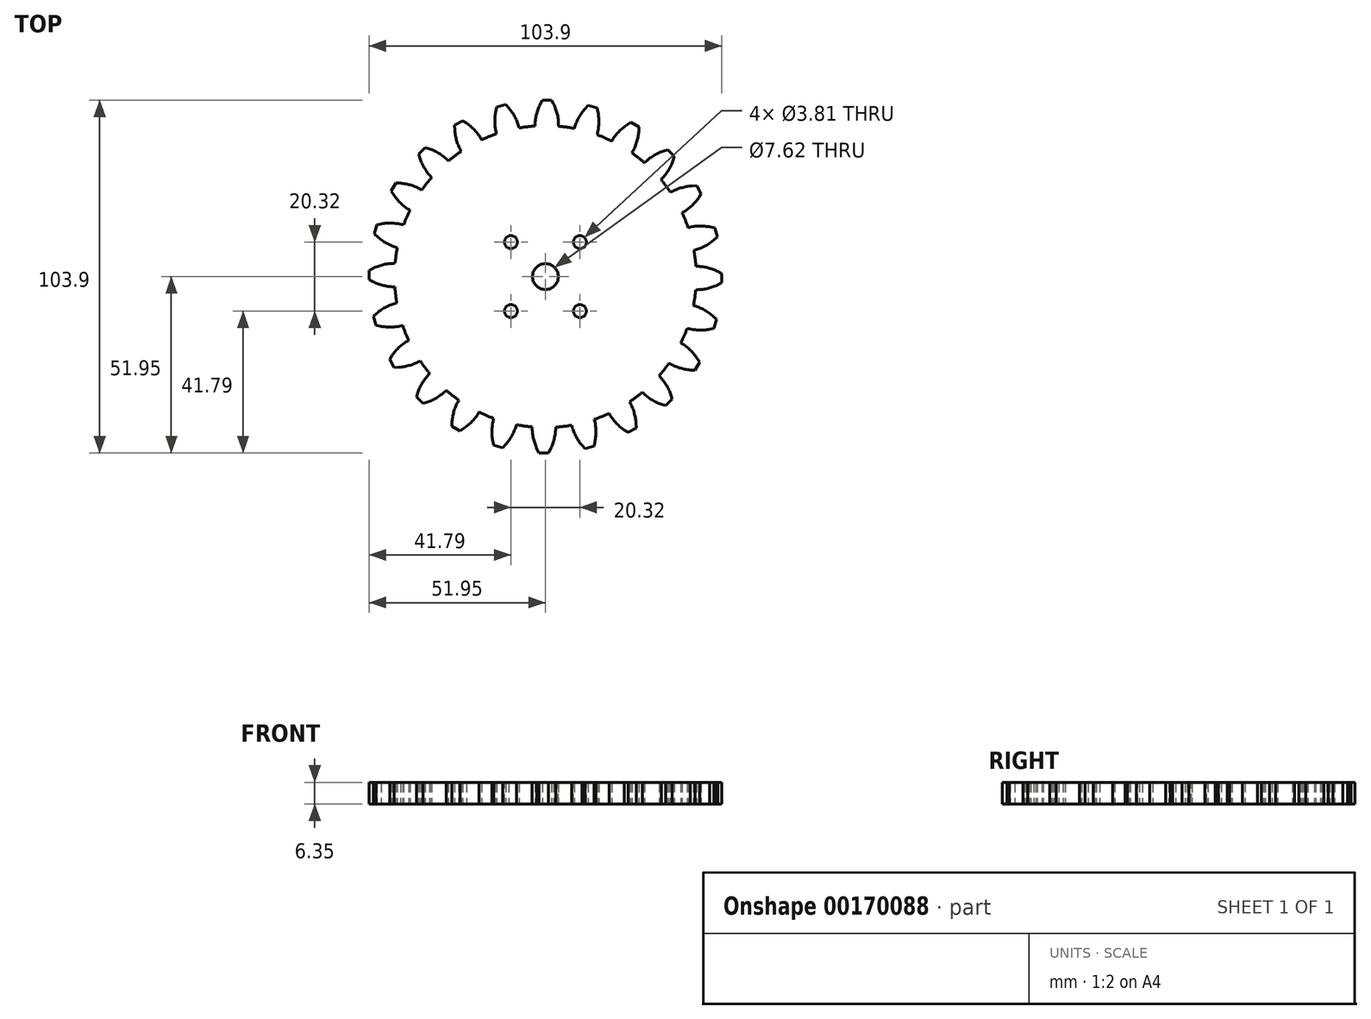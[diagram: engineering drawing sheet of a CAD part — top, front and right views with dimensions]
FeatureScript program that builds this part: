
annotation { "Feature Type Name" : "Feature", "Feature Type Description" : "" }
export const myFeature = defineFeature(function(context is Context, id is Id, definition is map)
    precondition{}
    {
        {
            var Q0;
            Q0=qCreatedBy(makeId("Top.planeOp"),FACE);
            var sketch = newSketch(context, id + "F0", { "sketchPlane" : qUnion([Q0])});
            skCircle(sketch, "E0", {"center": v(0, 0) * mm, "radius": 44.45 * mm});
            skCircle(sketch, "E1", {"center": v(0, 0) * mm, "radius": 47.63 * mm, "construction": true});
            skCircle(sketch, "E2", {"center": v(0, 0) * mm, "radius": 50.8 * mm, "construction": true});
            skLineSegment(sketch, "E3", {"start": v(74.5, -50.8) * mm, "end": v(0, 0) * mm, "construction": true});
            skLineSegment(sketch, "E4", {"start": v(0, 0) * mm, "end": v(77.18, -45.55) * mm, "construction": true});
            skLineSegment(sketch, "E5", {"start": v(39.35, -26.83) * mm, "end": v(73.48, 16.73) * mm, "construction": true});
            skLineSegment(sketch, "E6", {"start": v(39.35, -26.83) * mm, "end": v(56.8, 26.67) * mm, "construction": true});
            skCircle(sketch, "E7", {"center": v(39.35, -26.83) * mm, "radius": 14.6 * mm, "construction": true});
            skArc(sketch, "E8", {"start": v(36.25, -25.4) * mm, "mid": v(39.35, -26.84) * mm, "end": v(42.7, -27.5) * mm});
            skPoint(sketch, "E8.startSnap0", {"position": v(37.25, -25.4) * mm});
            skArc(sketch, "E9.MirrorCS", {"start": v(39.76, -19.45) * mm, "mid": v(42.52, -21.47) * mm, "end": v(44.73, -24.09) * mm});
            skLineSegment(sketch, "E10", {"start": v(44.73, -24.09) * mm, "end": v(45.45, -25.17) * mm});
            skLineSegment(sketch, "E11", {"start": v(45.45, -25.17) * mm, "end": v(44.04, -27.55) * mm});
            skLineSegment(sketch, "E12", {"start": v(44.04, -27.55) * mm, "end": v(42.7, -27.5) * mm});
            skArc(sketch, "E13.1.0", {"start": v(43.44, -8.5) * mm, "mid": v(46.63, -9.74) * mm, "end": v(49.44, -11.69) * mm});
            skLineSegment(sketch, "E13.1.1", {"start": v(49.44, -11.69) * mm, "end": v(50.41, -12.55) * mm});
            skLineSegment(sketch, "E13.1.2", {"start": v(50.41, -12.55) * mm, "end": v(49.67, -15.21) * mm});
            skLineSegment(sketch, "E13.1.3", {"start": v(49.67, -15.21) * mm, "end": v(48.37, -15.52) * mm});
            skArc(sketch, "E13.1.4", {"start": v(41.59, -15.16) * mm, "mid": v(44.96, -15.74) * mm, "end": v(48.37, -15.52) * mm});
            skArc(sketch, "E13.2.0", {"start": v(44.16, 3.04) * mm, "mid": v(47.56, 2.66) * mm, "end": v(50.78, 1.5) * mm});
            skLineSegment(sketch, "E13.2.1", {"start": v(50.78, 1.5) * mm, "end": v(51.95, 0.92) * mm});
            skLineSegment(sketch, "E13.2.2", {"start": v(51.95, 0.92) * mm, "end": v(51.92, -1.84) * mm});
            skLineSegment(sketch, "E13.2.3", {"start": v(51.92, -1.84) * mm, "end": v(50.74, -2.47) * mm});
            skArc(sketch, "E13.2.4", {"start": v(44.1, -3.88) * mm, "mid": v(47.5, -3.56) * mm, "end": v(50.74, -2.47) * mm});
            skArc(sketch, "E13.3.0", {"start": v(41.87, 14.36) * mm, "mid": v(45.25, 14.88) * mm, "end": v(48.66, 14.6) * mm});
            skLineSegment(sketch, "E13.3.1", {"start": v(48.66, 14.6) * mm, "end": v(49.94, 14.34) * mm});
            skLineSegment(sketch, "E13.3.2", {"start": v(49.94, 14.34) * mm, "end": v(50.63, 11.66) * mm});
            skLineSegment(sketch, "E13.3.3", {"start": v(50.63, 11.66) * mm, "end": v(49.65, 10.75) * mm});
            skArc(sketch, "E13.3.4", {"start": v(43.6, 7.67) * mm, "mid": v(46.8, 8.85) * mm, "end": v(49.65, 10.75) * mm});
            skArc(sketch, "E13.4.0", {"start": v(36.72, 24.71) * mm, "mid": v(39.86, 26.08) * mm, "end": v(43.22, 26.7) * mm});
            skLineSegment(sketch, "E13.4.1", {"start": v(43.22, 26.7) * mm, "end": v(44.52, 26.77) * mm});
            skLineSegment(sketch, "E13.4.2", {"start": v(44.52, 26.77) * mm, "end": v(45.88, 24.37) * mm});
            skLineSegment(sketch, "E13.4.3", {"start": v(45.88, 24.37) * mm, "end": v(45.18, 23.23) * mm});
            skArc(sketch, "E13.4.4", {"start": v(40.12, 18.7) * mm, "mid": v(42.92, 20.66) * mm, "end": v(45.18, 23.23) * mm});
            skArc(sketch, "E13.5.0", {"start": v(29.08, 33.37) * mm, "mid": v(31.75, 35.51) * mm, "end": v(34.84, 36.97) * mm});
            skLineSegment(sketch, "E13.5.1", {"start": v(34.84, 36.97) * mm, "end": v(36.08, 37.38) * mm});
            skLineSegment(sketch, "E13.5.2", {"start": v(36.08, 37.38) * mm, "end": v(38.01, 35.41) * mm});
            skLineSegment(sketch, "E13.5.3", {"start": v(38.01, 35.41) * mm, "end": v(37.62, 34.13) * mm});
            skArc(sketch, "E13.5.4", {"start": v(33.92, 28.44) * mm, "mid": v(36.1, 31.07) * mm, "end": v(37.62, 34.13) * mm});
            skArc(sketch, "E13.6.0", {"start": v(19.45, 39.76) * mm, "mid": v(21.47, 42.52) * mm, "end": v(24.09, 44.73) * mm});
            skLineSegment(sketch, "E13.6.1", {"start": v(24.09, 44.73) * mm, "end": v(25.17, 45.45) * mm});
            skLineSegment(sketch, "E13.6.2", {"start": v(25.17, 45.45) * mm, "end": v(27.55, 44.04) * mm});
            skLineSegment(sketch, "E13.6.3", {"start": v(27.55, 44.04) * mm, "end": v(27.5, 42.7) * mm});
            skArc(sketch, "E13.6.4", {"start": v(25.4, 36.25) * mm, "mid": v(26.84, 39.35) * mm, "end": v(27.5, 42.7) * mm});
            skArc(sketch, "E13.7.0", {"start": v(8.5, 43.44) * mm, "mid": v(9.74, 46.63) * mm, "end": v(11.69, 49.44) * mm});
            skLineSegment(sketch, "E13.7.1", {"start": v(11.69, 49.44) * mm, "end": v(12.55, 50.41) * mm});
            skLineSegment(sketch, "E13.7.2", {"start": v(12.55, 50.41) * mm, "end": v(15.21, 49.67) * mm});
            skLineSegment(sketch, "E13.7.3", {"start": v(15.21, 49.67) * mm, "end": v(15.52, 48.37) * mm});
            skArc(sketch, "E13.7.4", {"start": v(15.16, 41.59) * mm, "mid": v(15.74, 44.96) * mm, "end": v(15.52, 48.37) * mm});
            skArc(sketch, "E13.8.0", {"start": v(-3.04, 44.16) * mm, "mid": v(-2.66, 47.56) * mm, "end": v(-1.5, 50.78) * mm});
            skLineSegment(sketch, "E13.8.1", {"start": v(-1.5, 50.78) * mm, "end": v(-0.92, 51.95) * mm});
            skLineSegment(sketch, "E13.8.2", {"start": v(-0.92, 51.95) * mm, "end": v(1.84, 51.92) * mm});
            skLineSegment(sketch, "E13.8.3", {"start": v(1.84, 51.92) * mm, "end": v(2.47, 50.74) * mm});
            skArc(sketch, "E13.8.4", {"start": v(3.88, 44.1) * mm, "mid": v(3.56, 47.5) * mm, "end": v(2.47, 50.74) * mm});
            skArc(sketch, "E13.9.0", {"start": v(-14.36, 41.87) * mm, "mid": v(-14.88, 45.25) * mm, "end": v(-14.6, 48.66) * mm});
            skLineSegment(sketch, "E13.9.1", {"start": v(-14.6, 48.66) * mm, "end": v(-14.34, 49.94) * mm});
            skLineSegment(sketch, "E13.9.2", {"start": v(-14.34, 49.94) * mm, "end": v(-11.66, 50.63) * mm});
            skLineSegment(sketch, "E13.9.3", {"start": v(-11.66, 50.63) * mm, "end": v(-10.75, 49.65) * mm});
            skArc(sketch, "E13.9.4", {"start": v(-7.67, 43.6) * mm, "mid": v(-8.85, 46.8) * mm, "end": v(-10.75, 49.65) * mm});
            skArc(sketch, "E13.10.0", {"start": v(-24.71, 36.72) * mm, "mid": v(-26.08, 39.86) * mm, "end": v(-26.7, 43.22) * mm});
            skLineSegment(sketch, "E13.10.1", {"start": v(-26.7, 43.22) * mm, "end": v(-26.77, 44.52) * mm});
            skLineSegment(sketch, "E13.10.2", {"start": v(-26.77, 44.52) * mm, "end": v(-24.37, 45.88) * mm});
            skLineSegment(sketch, "E13.10.3", {"start": v(-24.37, 45.88) * mm, "end": v(-23.23, 45.18) * mm});
            skArc(sketch, "E13.10.4", {"start": v(-18.7, 40.12) * mm, "mid": v(-20.66, 42.92) * mm, "end": v(-23.23, 45.18) * mm});
            skArc(sketch, "E13.11.0", {"start": v(-33.37, 29.08) * mm, "mid": v(-35.51, 31.75) * mm, "end": v(-36.97, 34.84) * mm});
            skLineSegment(sketch, "E13.11.1", {"start": v(-36.97, 34.84) * mm, "end": v(-37.38, 36.08) * mm});
            skLineSegment(sketch, "E13.11.2", {"start": v(-37.38, 36.08) * mm, "end": v(-35.41, 38.01) * mm});
            skLineSegment(sketch, "E13.11.3", {"start": v(-35.41, 38.01) * mm, "end": v(-34.13, 37.62) * mm});
            skArc(sketch, "E13.11.4", {"start": v(-28.44, 33.92) * mm, "mid": v(-31.07, 36.1) * mm, "end": v(-34.13, 37.62) * mm});
            skArc(sketch, "E13.12.0", {"start": v(-39.76, 19.45) * mm, "mid": v(-42.52, 21.47) * mm, "end": v(-44.73, 24.09) * mm});
            skLineSegment(sketch, "E13.12.1", {"start": v(-44.73, 24.09) * mm, "end": v(-45.45, 25.17) * mm});
            skLineSegment(sketch, "E13.12.2", {"start": v(-45.45, 25.17) * mm, "end": v(-44.04, 27.55) * mm});
            skLineSegment(sketch, "E13.12.3", {"start": v(-44.04, 27.55) * mm, "end": v(-42.7, 27.5) * mm});
            skArc(sketch, "E13.12.4", {"start": v(-36.25, 25.4) * mm, "mid": v(-39.35, 26.84) * mm, "end": v(-42.7, 27.5) * mm});
            skArc(sketch, "E13.13.0", {"start": v(-43.44, 8.5) * mm, "mid": v(-46.63, 9.74) * mm, "end": v(-49.44, 11.69) * mm});
            skLineSegment(sketch, "E13.13.1", {"start": v(-49.44, 11.69) * mm, "end": v(-50.41, 12.55) * mm});
            skLineSegment(sketch, "E13.13.2", {"start": v(-50.41, 12.55) * mm, "end": v(-49.67, 15.21) * mm});
            skLineSegment(sketch, "E13.13.3", {"start": v(-49.67, 15.21) * mm, "end": v(-48.37, 15.52) * mm});
            skArc(sketch, "E13.13.4", {"start": v(-41.59, 15.16) * mm, "mid": v(-44.96, 15.74) * mm, "end": v(-48.37, 15.52) * mm});
            skArc(sketch, "E13.14.0", {"start": v(-44.16, -3.04) * mm, "mid": v(-47.56, -2.66) * mm, "end": v(-50.78, -1.5) * mm});
            skLineSegment(sketch, "E13.14.1", {"start": v(-50.78, -1.5) * mm, "end": v(-51.95, -0.92) * mm});
            skLineSegment(sketch, "E13.14.2", {"start": v(-51.95, -0.92) * mm, "end": v(-51.92, 1.84) * mm});
            skLineSegment(sketch, "E13.14.3", {"start": v(-51.92, 1.84) * mm, "end": v(-50.74, 2.47) * mm});
            skArc(sketch, "E13.14.4", {"start": v(-44.1, 3.88) * mm, "mid": v(-47.5, 3.56) * mm, "end": v(-50.74, 2.47) * mm});
            skArc(sketch, "E13.15.0", {"start": v(-41.87, -14.36) * mm, "mid": v(-45.25, -14.88) * mm, "end": v(-48.66, -14.6) * mm});
            skLineSegment(sketch, "E13.15.1", {"start": v(-48.66, -14.6) * mm, "end": v(-49.94, -14.34) * mm});
            skLineSegment(sketch, "E13.15.2", {"start": v(-49.94, -14.34) * mm, "end": v(-50.63, -11.66) * mm});
            skLineSegment(sketch, "E13.15.3", {"start": v(-50.63, -11.66) * mm, "end": v(-49.65, -10.75) * mm});
            skArc(sketch, "E13.15.4", {"start": v(-43.6, -7.67) * mm, "mid": v(-46.8, -8.85) * mm, "end": v(-49.65, -10.75) * mm});
            skArc(sketch, "E13.16.0", {"start": v(-36.72, -24.71) * mm, "mid": v(-39.86, -26.08) * mm, "end": v(-43.22, -26.7) * mm});
            skLineSegment(sketch, "E13.16.1", {"start": v(-43.22, -26.7) * mm, "end": v(-44.52, -26.77) * mm});
            skLineSegment(sketch, "E13.16.2", {"start": v(-44.52, -26.77) * mm, "end": v(-45.88, -24.37) * mm});
            skLineSegment(sketch, "E13.16.3", {"start": v(-45.88, -24.37) * mm, "end": v(-45.18, -23.23) * mm});
            skArc(sketch, "E13.16.4", {"start": v(-40.12, -18.7) * mm, "mid": v(-42.92, -20.66) * mm, "end": v(-45.18, -23.23) * mm});
            skArc(sketch, "E13.17.0", {"start": v(-29.08, -33.37) * mm, "mid": v(-31.75, -35.51) * mm, "end": v(-34.84, -36.97) * mm});
            skLineSegment(sketch, "E13.17.1", {"start": v(-34.84, -36.97) * mm, "end": v(-36.08, -37.38) * mm});
            skLineSegment(sketch, "E13.17.2", {"start": v(-36.08, -37.38) * mm, "end": v(-38.01, -35.41) * mm});
            skLineSegment(sketch, "E13.17.3", {"start": v(-38.01, -35.41) * mm, "end": v(-37.62, -34.13) * mm});
            skArc(sketch, "E13.17.4", {"start": v(-33.92, -28.44) * mm, "mid": v(-36.1, -31.07) * mm, "end": v(-37.62, -34.13) * mm});
            skArc(sketch, "E13.18.0", {"start": v(-19.45, -39.76) * mm, "mid": v(-21.47, -42.52) * mm, "end": v(-24.09, -44.73) * mm});
            skLineSegment(sketch, "E13.18.1", {"start": v(-24.09, -44.73) * mm, "end": v(-25.17, -45.45) * mm});
            skLineSegment(sketch, "E13.18.2", {"start": v(-25.17, -45.45) * mm, "end": v(-27.55, -44.04) * mm});
            skLineSegment(sketch, "E13.18.3", {"start": v(-27.55, -44.04) * mm, "end": v(-27.5, -42.7) * mm});
            skArc(sketch, "E13.18.4", {"start": v(-25.4, -36.25) * mm, "mid": v(-26.84, -39.35) * mm, "end": v(-27.5, -42.7) * mm});
            skArc(sketch, "E13.19.0", {"start": v(-8.5, -43.44) * mm, "mid": v(-9.74, -46.63) * mm, "end": v(-11.69, -49.44) * mm});
            skLineSegment(sketch, "E13.19.1", {"start": v(-11.69, -49.44) * mm, "end": v(-12.55, -50.41) * mm});
            skLineSegment(sketch, "E13.19.2", {"start": v(-12.55, -50.41) * mm, "end": v(-15.21, -49.67) * mm});
            skLineSegment(sketch, "E13.19.3", {"start": v(-15.21, -49.67) * mm, "end": v(-15.52, -48.37) * mm});
            skArc(sketch, "E13.19.4", {"start": v(-15.16, -41.59) * mm, "mid": v(-15.74, -44.96) * mm, "end": v(-15.52, -48.37) * mm});
            skArc(sketch, "E13.20.0", {"start": v(3.04, -44.16) * mm, "mid": v(2.66, -47.56) * mm, "end": v(1.5, -50.78) * mm});
            skLineSegment(sketch, "E13.20.1", {"start": v(1.5, -50.78) * mm, "end": v(0.92, -51.95) * mm});
            skLineSegment(sketch, "E13.20.2", {"start": v(0.92, -51.95) * mm, "end": v(-1.84, -51.92) * mm});
            skLineSegment(sketch, "E13.20.3", {"start": v(-1.84, -51.92) * mm, "end": v(-2.47, -50.74) * mm});
            skArc(sketch, "E13.20.4", {"start": v(-3.88, -44.1) * mm, "mid": v(-3.56, -47.5) * mm, "end": v(-2.47, -50.74) * mm});
            skArc(sketch, "E13.21.0", {"start": v(14.36, -41.87) * mm, "mid": v(14.88, -45.25) * mm, "end": v(14.6, -48.66) * mm});
            skLineSegment(sketch, "E13.21.1", {"start": v(14.6, -48.66) * mm, "end": v(14.34, -49.94) * mm});
            skLineSegment(sketch, "E13.21.2", {"start": v(14.34, -49.94) * mm, "end": v(11.66, -50.63) * mm});
            skLineSegment(sketch, "E13.21.3", {"start": v(11.66, -50.63) * mm, "end": v(10.75, -49.65) * mm});
            skArc(sketch, "E13.21.4", {"start": v(7.67, -43.6) * mm, "mid": v(8.85, -46.8) * mm, "end": v(10.75, -49.65) * mm});
            skArc(sketch, "E13.22.0", {"start": v(24.71, -36.72) * mm, "mid": v(26.08, -39.86) * mm, "end": v(26.7, -43.22) * mm});
            skLineSegment(sketch, "E13.22.1", {"start": v(26.7, -43.22) * mm, "end": v(26.77, -44.52) * mm});
            skLineSegment(sketch, "E13.22.2", {"start": v(26.77, -44.52) * mm, "end": v(24.37, -45.88) * mm});
            skLineSegment(sketch, "E13.22.3", {"start": v(24.37, -45.88) * mm, "end": v(23.23, -45.18) * mm});
            skArc(sketch, "E13.22.4", {"start": v(18.7, -40.12) * mm, "mid": v(20.66, -42.92) * mm, "end": v(23.23, -45.18) * mm});
            skArc(sketch, "E13.23.0", {"start": v(33.37, -29.08) * mm, "mid": v(35.51, -31.75) * mm, "end": v(36.97, -34.84) * mm});
            skLineSegment(sketch, "E13.23.1", {"start": v(36.97, -34.84) * mm, "end": v(37.38, -36.08) * mm});
            skLineSegment(sketch, "E13.23.2", {"start": v(37.38, -36.08) * mm, "end": v(35.41, -38.01) * mm});
            skLineSegment(sketch, "E13.23.3", {"start": v(35.41, -38.01) * mm, "end": v(34.13, -37.62) * mm});
            skArc(sketch, "E13.23.4", {"start": v(28.44, -33.92) * mm, "mid": v(31.07, -36.1) * mm, "end": v(34.13, -37.62) * mm});
            skSolve(sketch);
        }
        {
            var Q0;
            {var subQ0=sQuery(id+"F0.wireOp",EDGE,"E0");var subQ30=makeQuery(id+"F0.imprint","INTERSECT",VERTEX,{"derivedFrom":[subQ0,sQuery(id+"F0.wireOp",EDGE,"E13.3.4")]});Q0=makeQuery(id+"F0.imprint","IMPRINT",FACE,{"disambiguationData":[TD([[makeQuery(id+"F0.imprint","IMPRINT",EDGE,{"disambiguationData":[TD([[subQ30,1.0]])],"derivedFrom":subQ0}),1.0]])]});}
            var Q1;
            {var subQ5=sQuery(id+"F0.wireOp",EDGE,"E13.13.1");Q1=makeQuery(id+"F0.imprint","IMPRINT",FACE,{"disambiguationData":[TD([[makeQuery(id+"F0.imprint","IMPRINT",EDGE,{"derivedFrom":subQ5}),-1.0]])]});}
            var Q2;
            {var subQ0=sQuery(id+"F0.wireOp",EDGE,"E13.12.1");Q2=makeQuery(id+"F0.imprint","IMPRINT",FACE,{"disambiguationData":[TD([[makeQuery(id+"F0.imprint","IMPRINT",EDGE,{"derivedFrom":subQ0}),-1.0]])]});}
            var Q3;
            {var subQ0=sQuery(id+"F0.wireOp",EDGE,"E13.11.1");Q3=makeQuery(id+"F0.imprint","IMPRINT",FACE,{"disambiguationData":[TD([[makeQuery(id+"F0.imprint","IMPRINT",EDGE,{"derivedFrom":subQ0}),-1.0]])]});}
            var Q4;
            {var subQ0=sQuery(id+"F0.wireOp",EDGE,"E13.10.1");Q4=makeQuery(id+"F0.imprint","IMPRINT",FACE,{"disambiguationData":[TD([[makeQuery(id+"F0.imprint","IMPRINT",EDGE,{"derivedFrom":subQ0}),-1.0]])]});}
            var Q5;
            {var subQ0=sQuery(id+"F0.wireOp",EDGE,"E13.9.1");Q5=makeQuery(id+"F0.imprint","IMPRINT",FACE,{"disambiguationData":[TD([[makeQuery(id+"F0.imprint","IMPRINT",EDGE,{"derivedFrom":subQ0}),-1.0]])]});}
            var Q6;
            {var subQ0=sQuery(id+"F0.wireOp",EDGE,"E13.8.1");Q6=makeQuery(id+"F0.imprint","IMPRINT",FACE,{"disambiguationData":[TD([[makeQuery(id+"F0.imprint","IMPRINT",EDGE,{"derivedFrom":subQ0}),-1.0]])]});}
            var Q7;
            {var subQ5=sQuery(id+"F0.wireOp",EDGE,"E13.7.1");Q7=makeQuery(id+"F0.imprint","IMPRINT",FACE,{"disambiguationData":[TD([[makeQuery(id+"F0.imprint","IMPRINT",EDGE,{"derivedFrom":subQ5}),-1.0]])]});}
            var Q8;
            {var subQ0=sQuery(id+"F0.wireOp",EDGE,"E13.6.1");Q8=makeQuery(id+"F0.imprint","IMPRINT",FACE,{"disambiguationData":[TD([[makeQuery(id+"F0.imprint","IMPRINT",EDGE,{"derivedFrom":subQ0}),-1.0]])]});}
            var Q9;
            {var subQ0=sQuery(id+"F0.wireOp",EDGE,"E13.5.1");Q9=makeQuery(id+"F0.imprint","IMPRINT",FACE,{"disambiguationData":[TD([[makeQuery(id+"F0.imprint","IMPRINT",EDGE,{"derivedFrom":subQ0}),-1.0]])]});}
            var Q10;
            {var subQ0=sQuery(id+"F0.wireOp",EDGE,"E13.4.1");Q10=makeQuery(id+"F0.imprint","IMPRINT",FACE,{"disambiguationData":[TD([[makeQuery(id+"F0.imprint","IMPRINT",EDGE,{"derivedFrom":subQ0}),-1.0]])]});}
            var Q11;
            {var subQ0=sQuery(id+"F0.wireOp",EDGE,"E13.3.1");Q11=makeQuery(id+"F0.imprint","IMPRINT",FACE,{"disambiguationData":[TD([[makeQuery(id+"F0.imprint","IMPRINT",EDGE,{"derivedFrom":subQ0}),-1.0]])]});}
            var Q12;
            {var subQ5=sQuery(id+"F0.wireOp",EDGE,"E13.2.1");Q12=makeQuery(id+"F0.imprint","IMPRINT",FACE,{"disambiguationData":[TD([[makeQuery(id+"F0.imprint","IMPRINT",EDGE,{"derivedFrom":subQ5}),-1.0]])]});}
            var Q13;
            {var subQ0=sQuery(id+"F0.wireOp",EDGE,"E13.1.1");Q13=makeQuery(id+"F0.imprint","IMPRINT",FACE,{"disambiguationData":[TD([[makeQuery(id+"F0.imprint","IMPRINT",EDGE,{"derivedFrom":subQ0}),-1.0]])]});}
            var Q14;
            {var subQ0=sQuery(id+"F0.wireOp",EDGE,"E10");Q14=makeQuery(id+"F0.imprint","IMPRINT",FACE,{"disambiguationData":[TD([[makeQuery(id+"F0.imprint","IMPRINT",EDGE,{"derivedFrom":subQ0}),-1.0]])]});}
            var Q15;
            {var subQ0=sQuery(id+"F0.wireOp",EDGE,"E13.23.1");Q15=makeQuery(id+"F0.imprint","IMPRINT",FACE,{"disambiguationData":[TD([[makeQuery(id+"F0.imprint","IMPRINT",EDGE,{"derivedFrom":subQ0}),-1.0]])]});}
            var Q16;
            {var subQ0=sQuery(id+"F0.wireOp",EDGE,"E13.22.1");Q16=makeQuery(id+"F0.imprint","IMPRINT",FACE,{"disambiguationData":[TD([[makeQuery(id+"F0.imprint","IMPRINT",EDGE,{"derivedFrom":subQ0}),-1.0]])]});}
            var Q17;
            {var subQ0=sQuery(id+"F0.wireOp",EDGE,"E13.21.1");Q17=makeQuery(id+"F0.imprint","IMPRINT",FACE,{"disambiguationData":[TD([[makeQuery(id+"F0.imprint","IMPRINT",EDGE,{"derivedFrom":subQ0}),-1.0]])]});}
            var Q18;
            {var subQ0=sQuery(id+"F0.wireOp",EDGE,"E13.20.1");Q18=makeQuery(id+"F0.imprint","IMPRINT",FACE,{"disambiguationData":[TD([[makeQuery(id+"F0.imprint","IMPRINT",EDGE,{"derivedFrom":subQ0}),-1.0]])]});}
            var Q19;
            {var subQ0=sQuery(id+"F0.wireOp",EDGE,"E13.19.1");Q19=makeQuery(id+"F0.imprint","IMPRINT",FACE,{"disambiguationData":[TD([[makeQuery(id+"F0.imprint","IMPRINT",EDGE,{"derivedFrom":subQ0}),-1.0]])]});}
            var Q20;
            {var subQ0=sQuery(id+"F0.wireOp",EDGE,"E13.18.1");Q20=makeQuery(id+"F0.imprint","IMPRINT",FACE,{"disambiguationData":[TD([[makeQuery(id+"F0.imprint","IMPRINT",EDGE,{"derivedFrom":subQ0}),-1.0]])]});}
            var Q21;
            {var subQ0=sQuery(id+"F0.wireOp",EDGE,"E13.17.1");Q21=makeQuery(id+"F0.imprint","IMPRINT",FACE,{"disambiguationData":[TD([[makeQuery(id+"F0.imprint","IMPRINT",EDGE,{"derivedFrom":subQ0}),-1.0]])]});}
            var Q22;
            {var subQ0=sQuery(id+"F0.wireOp",EDGE,"E13.16.1");Q22=makeQuery(id+"F0.imprint","IMPRINT",FACE,{"disambiguationData":[TD([[makeQuery(id+"F0.imprint","IMPRINT",EDGE,{"derivedFrom":subQ0}),-1.0]])]});}
            var Q23;
            {var subQ0=sQuery(id+"F0.wireOp",EDGE,"E13.15.1");Q23=makeQuery(id+"F0.imprint","IMPRINT",FACE,{"disambiguationData":[TD([[makeQuery(id+"F0.imprint","IMPRINT",EDGE,{"derivedFrom":subQ0}),-1.0]])]});}
            var Q24;
            {var subQ0=sQuery(id+"F0.wireOp",EDGE,"E13.14.1");Q24=makeQuery(id+"F0.imprint","IMPRINT",FACE,{"disambiguationData":[TD([[makeQuery(id+"F0.imprint","IMPRINT",EDGE,{"derivedFrom":subQ0}),-1.0]])]});}
            extrude(context, id + "F1", {"entities" : qUnion([Q0, Q1, Q2, Q3, Q4, Q5, Q6, Q7, Q8, Q9, Q10, Q11, Q12, Q13, Q14, Q15, Q16, Q17, Q18, Q19, Q20, Q21, Q22, Q23, Q24]), "depth" : 6.35 * mm});
        }
        {
            var Q0;
            Q0=makeQuery(id+"F1.opExtrude","CAP_FACE",FACE,{"disambiguationData":[OSD([sQuery(id+"F0.wireOp",EDGE,"E0"),sQuery(id+"F0.wireOp",EDGE,"E8"),sQuery(id+"F0.wireOp",EDGE,"E9.MirrorCS"),sQuery(id+"F0.wireOp",EDGE,"E10"),sQuery(id+"F0.wireOp",EDGE,"E11"),sQuery(id+"F0.wireOp",EDGE,"E12"),sQuery(id+"F0.wireOp",EDGE,"E13.1.0"),sQuery(id+"F0.wireOp",EDGE,"E13.1.1"),sQuery(id+"F0.wireOp",EDGE,"E13.1.2"),sQuery(id+"F0.wireOp",EDGE,"E13.1.3"),sQuery(id+"F0.wireOp",EDGE,"E13.1.4"),sQuery(id+"F0.wireOp",EDGE,"E13.2.0"),sQuery(id+"F0.wireOp",EDGE,"E13.2.1"),sQuery(id+"F0.wireOp",EDGE,"E13.2.2"),sQuery(id+"F0.wireOp",EDGE,"E13.2.3"),sQuery(id+"F0.wireOp",EDGE,"E13.2.4"),sQuery(id+"F0.wireOp",EDGE,"E13.3.0"),sQuery(id+"F0.wireOp",EDGE,"E13.3.1"),sQuery(id+"F0.wireOp",EDGE,"E13.3.2"),sQuery(id+"F0.wireOp",EDGE,"E13.3.3"),sQuery(id+"F0.wireOp",EDGE,"E13.3.4"),sQuery(id+"F0.wireOp",EDGE,"E13.4.0"),sQuery(id+"F0.wireOp",EDGE,"E13.4.1"),sQuery(id+"F0.wireOp",EDGE,"E13.4.2"),sQuery(id+"F0.wireOp",EDGE,"E13.4.3"),sQuery(id+"F0.wireOp",EDGE,"E13.4.4"),sQuery(id+"F0.wireOp",EDGE,"E13.5.0"),sQuery(id+"F0.wireOp",EDGE,"E13.5.1"),sQuery(id+"F0.wireOp",EDGE,"E13.5.2"),sQuery(id+"F0.wireOp",EDGE,"E13.5.3"),sQuery(id+"F0.wireOp",EDGE,"E13.5.4"),sQuery(id+"F0.wireOp",EDGE,"E13.6.0"),sQuery(id+"F0.wireOp",EDGE,"E13.6.1"),sQuery(id+"F0.wireOp",EDGE,"E13.6.2"),sQuery(id+"F0.wireOp",EDGE,"E13.6.3"),sQuery(id+"F0.wireOp",EDGE,"E13.6.4"),sQuery(id+"F0.wireOp",EDGE,"E13.7.0"),sQuery(id+"F0.wireOp",EDGE,"E13.7.1"),sQuery(id+"F0.wireOp",EDGE,"E13.7.2"),sQuery(id+"F0.wireOp",EDGE,"E13.7.3"),sQuery(id+"F0.wireOp",EDGE,"E13.7.4"),sQuery(id+"F0.wireOp",EDGE,"E13.8.0"),sQuery(id+"F0.wireOp",EDGE,"E13.8.1"),sQuery(id+"F0.wireOp",EDGE,"E13.8.2"),sQuery(id+"F0.wireOp",EDGE,"E13.8.3"),sQuery(id+"F0.wireOp",EDGE,"E13.8.4"),sQuery(id+"F0.wireOp",EDGE,"E13.9.0"),sQuery(id+"F0.wireOp",EDGE,"E13.9.1"),sQuery(id+"F0.wireOp",EDGE,"E13.9.2"),sQuery(id+"F0.wireOp",EDGE,"E13.9.3"),sQuery(id+"F0.wireOp",EDGE,"E13.9.4"),sQuery(id+"F0.wireOp",EDGE,"E13.10.0"),sQuery(id+"F0.wireOp",EDGE,"E13.10.1"),sQuery(id+"F0.wireOp",EDGE,"E13.10.2"),sQuery(id+"F0.wireOp",EDGE,"E13.10.3"),sQuery(id+"F0.wireOp",EDGE,"E13.10.4"),sQuery(id+"F0.wireOp",EDGE,"E13.11.0"),sQuery(id+"F0.wireOp",EDGE,"E13.11.1"),sQuery(id+"F0.wireOp",EDGE,"E13.11.2"),sQuery(id+"F0.wireOp",EDGE,"E13.11.3"),sQuery(id+"F0.wireOp",EDGE,"E13.11.4"),sQuery(id+"F0.wireOp",EDGE,"E13.12.0"),sQuery(id+"F0.wireOp",EDGE,"E13.12.1"),sQuery(id+"F0.wireOp",EDGE,"E13.12.2"),sQuery(id+"F0.wireOp",EDGE,"E13.12.3"),sQuery(id+"F0.wireOp",EDGE,"E13.12.4"),sQuery(id+"F0.wireOp",EDGE,"E13.13.0"),sQuery(id+"F0.wireOp",EDGE,"E13.13.1"),sQuery(id+"F0.wireOp",EDGE,"E13.13.2"),sQuery(id+"F0.wireOp",EDGE,"E13.13.3"),sQuery(id+"F0.wireOp",EDGE,"E13.13.4"),sQuery(id+"F0.wireOp",EDGE,"E13.14.0"),sQuery(id+"F0.wireOp",EDGE,"E13.14.1"),sQuery(id+"F0.wireOp",EDGE,"E13.14.2"),sQuery(id+"F0.wireOp",EDGE,"E13.14.3"),sQuery(id+"F0.wireOp",EDGE,"E13.14.4"),sQuery(id+"F0.wireOp",EDGE,"E13.15.0"),sQuery(id+"F0.wireOp",EDGE,"E13.15.1"),sQuery(id+"F0.wireOp",EDGE,"E13.15.2"),sQuery(id+"F0.wireOp",EDGE,"E13.15.3"),sQuery(id+"F0.wireOp",EDGE,"E13.15.4"),sQuery(id+"F0.wireOp",EDGE,"E13.16.0"),sQuery(id+"F0.wireOp",EDGE,"E13.16.1"),sQuery(id+"F0.wireOp",EDGE,"E13.16.2"),sQuery(id+"F0.wireOp",EDGE,"E13.16.3"),sQuery(id+"F0.wireOp",EDGE,"E13.16.4"),sQuery(id+"F0.wireOp",EDGE,"E13.17.0"),sQuery(id+"F0.wireOp",EDGE,"E13.17.1"),sQuery(id+"F0.wireOp",EDGE,"E13.17.2"),sQuery(id+"F0.wireOp",EDGE,"E13.17.3"),sQuery(id+"F0.wireOp",EDGE,"E13.17.4"),sQuery(id+"F0.wireOp",EDGE,"E13.18.0"),sQuery(id+"F0.wireOp",EDGE,"E13.18.1"),sQuery(id+"F0.wireOp",EDGE,"E13.18.2"),sQuery(id+"F0.wireOp",EDGE,"E13.18.3"),sQuery(id+"F0.wireOp",EDGE,"E13.18.4"),sQuery(id+"F0.wireOp",EDGE,"E13.19.0"),sQuery(id+"F0.wireOp",EDGE,"E13.19.1"),sQuery(id+"F0.wireOp",EDGE,"E13.19.2"),sQuery(id+"F0.wireOp",EDGE,"E13.19.3"),sQuery(id+"F0.wireOp",EDGE,"E13.19.4"),sQuery(id+"F0.wireOp",EDGE,"E13.20.0"),sQuery(id+"F0.wireOp",EDGE,"E13.20.1"),sQuery(id+"F0.wireOp",EDGE,"E13.20.2"),sQuery(id+"F0.wireOp",EDGE,"E13.20.3"),sQuery(id+"F0.wireOp",EDGE,"E13.20.4"),sQuery(id+"F0.wireOp",EDGE,"E13.21.0"),sQuery(id+"F0.wireOp",EDGE,"E13.21.1"),sQuery(id+"F0.wireOp",EDGE,"E13.21.2"),sQuery(id+"F0.wireOp",EDGE,"E13.21.3"),sQuery(id+"F0.wireOp",EDGE,"E13.21.4"),sQuery(id+"F0.wireOp",EDGE,"E13.22.0"),sQuery(id+"F0.wireOp",EDGE,"E13.22.1"),sQuery(id+"F0.wireOp",EDGE,"E13.22.2"),sQuery(id+"F0.wireOp",EDGE,"E13.22.3"),sQuery(id+"F0.wireOp",EDGE,"E13.22.4"),sQuery(id+"F0.wireOp",EDGE,"E13.23.0"),sQuery(id+"F0.wireOp",EDGE,"E13.23.1"),sQuery(id+"F0.wireOp",EDGE,"E13.23.2"),sQuery(id+"F0.wireOp",EDGE,"E13.23.3"),sQuery(id+"F0.wireOp",EDGE,"E13.23.4")])],"isStart":false});
            var sketch = newSketch(context, id + "F2", { "sketchPlane" : qUnion([Q0])});
            skLineSegment(sketch, "E14.bottom", {"start": v(10.16, 10.16) * mm, "end": v(-10.16, 10.16) * mm});
            skLineSegment(sketch, "E14.top", {"start": v(10.16, -10.16) * mm, "end": v(-10.16, -10.16) * mm});
            skLineSegment(sketch, "E14.left", {"start": v(10.16, 10.16) * mm, "end": v(10.16, -10.16) * mm});
            skLineSegment(sketch, "E14.right", {"start": v(-10.16, 10.16) * mm, "end": v(-10.16, -10.16) * mm});
            skPoint(sketch, "E14.middle", {"position": v(0, 0) * mm});
            skPoint(sketch, "E15", {"position": v(-10.16, 10.16) * mm});
            skPoint(sketch, "E16", {"position": v(-10.16, -10.16) * mm});
            skPoint(sketch, "E17", {"position": v(10.16, -10.16) * mm});
            skPoint(sketch, "E18", {"position": v(10.16, 10.16) * mm});
            skSolve(sketch);
        }
        {
            var Q0;
            Q0=sQuery(id+"F2.wireOp",VERTEX,"E15");
            var Q1;
            Q1=sQuery(id+"F2.wireOp",VERTEX,"E18");
            var Q2;
            Q2=sQuery(id+"F2.wireOp",VERTEX,"E16");
            var Q3;
            Q3=sQuery(id+"F2.wireOp",VERTEX,"E17");
            var Q4;
            Q4=makeQuery(id+"F1.opExtrude","SWEPT_BODY",BODY,{"disambiguationData":[OSD([sQuery(id+"F0.wireOp",EDGE,"E0"),sQuery(id+"F0.wireOp",EDGE,"E8"),sQuery(id+"F0.wireOp",EDGE,"E9.MirrorCS"),sQuery(id+"F0.wireOp",EDGE,"E10"),sQuery(id+"F0.wireOp",EDGE,"E11"),sQuery(id+"F0.wireOp",EDGE,"E12"),sQuery(id+"F0.wireOp",EDGE,"E13.1.0"),sQuery(id+"F0.wireOp",EDGE,"E13.1.1"),sQuery(id+"F0.wireOp",EDGE,"E13.1.2"),sQuery(id+"F0.wireOp",EDGE,"E13.1.3"),sQuery(id+"F0.wireOp",EDGE,"E13.1.4"),sQuery(id+"F0.wireOp",EDGE,"E13.2.0"),sQuery(id+"F0.wireOp",EDGE,"E13.2.1"),sQuery(id+"F0.wireOp",EDGE,"E13.2.2"),sQuery(id+"F0.wireOp",EDGE,"E13.2.3"),sQuery(id+"F0.wireOp",EDGE,"E13.2.4"),sQuery(id+"F0.wireOp",EDGE,"E13.3.0"),sQuery(id+"F0.wireOp",EDGE,"E13.3.1"),sQuery(id+"F0.wireOp",EDGE,"E13.3.2"),sQuery(id+"F0.wireOp",EDGE,"E13.3.3"),sQuery(id+"F0.wireOp",EDGE,"E13.3.4"),sQuery(id+"F0.wireOp",EDGE,"E13.4.0"),sQuery(id+"F0.wireOp",EDGE,"E13.4.1"),sQuery(id+"F0.wireOp",EDGE,"E13.4.2"),sQuery(id+"F0.wireOp",EDGE,"E13.4.3"),sQuery(id+"F0.wireOp",EDGE,"E13.4.4"),sQuery(id+"F0.wireOp",EDGE,"E13.5.0"),sQuery(id+"F0.wireOp",EDGE,"E13.5.1"),sQuery(id+"F0.wireOp",EDGE,"E13.5.2"),sQuery(id+"F0.wireOp",EDGE,"E13.5.3"),sQuery(id+"F0.wireOp",EDGE,"E13.5.4"),sQuery(id+"F0.wireOp",EDGE,"E13.6.0"),sQuery(id+"F0.wireOp",EDGE,"E13.6.1"),sQuery(id+"F0.wireOp",EDGE,"E13.6.2"),sQuery(id+"F0.wireOp",EDGE,"E13.6.3"),sQuery(id+"F0.wireOp",EDGE,"E13.6.4"),sQuery(id+"F0.wireOp",EDGE,"E13.7.0"),sQuery(id+"F0.wireOp",EDGE,"E13.7.1"),sQuery(id+"F0.wireOp",EDGE,"E13.7.2"),sQuery(id+"F0.wireOp",EDGE,"E13.7.3"),sQuery(id+"F0.wireOp",EDGE,"E13.7.4"),sQuery(id+"F0.wireOp",EDGE,"E13.8.0"),sQuery(id+"F0.wireOp",EDGE,"E13.8.1"),sQuery(id+"F0.wireOp",EDGE,"E13.8.2"),sQuery(id+"F0.wireOp",EDGE,"E13.8.3"),sQuery(id+"F0.wireOp",EDGE,"E13.8.4"),sQuery(id+"F0.wireOp",EDGE,"E13.9.0"),sQuery(id+"F0.wireOp",EDGE,"E13.9.1"),sQuery(id+"F0.wireOp",EDGE,"E13.9.2"),sQuery(id+"F0.wireOp",EDGE,"E13.9.3"),sQuery(id+"F0.wireOp",EDGE,"E13.9.4"),sQuery(id+"F0.wireOp",EDGE,"E13.10.0"),sQuery(id+"F0.wireOp",EDGE,"E13.10.1"),sQuery(id+"F0.wireOp",EDGE,"E13.10.2"),sQuery(id+"F0.wireOp",EDGE,"E13.10.3"),sQuery(id+"F0.wireOp",EDGE,"E13.10.4"),sQuery(id+"F0.wireOp",EDGE,"E13.11.0"),sQuery(id+"F0.wireOp",EDGE,"E13.11.1"),sQuery(id+"F0.wireOp",EDGE,"E13.11.2"),sQuery(id+"F0.wireOp",EDGE,"E13.11.3"),sQuery(id+"F0.wireOp",EDGE,"E13.11.4"),sQuery(id+"F0.wireOp",EDGE,"E13.12.0"),sQuery(id+"F0.wireOp",EDGE,"E13.12.1"),sQuery(id+"F0.wireOp",EDGE,"E13.12.2"),sQuery(id+"F0.wireOp",EDGE,"E13.12.3"),sQuery(id+"F0.wireOp",EDGE,"E13.12.4"),sQuery(id+"F0.wireOp",EDGE,"E13.13.0"),sQuery(id+"F0.wireOp",EDGE,"E13.13.1"),sQuery(id+"F0.wireOp",EDGE,"E13.13.2"),sQuery(id+"F0.wireOp",EDGE,"E13.13.3"),sQuery(id+"F0.wireOp",EDGE,"E13.13.4"),sQuery(id+"F0.wireOp",EDGE,"E13.14.0"),sQuery(id+"F0.wireOp",EDGE,"E13.14.1"),sQuery(id+"F0.wireOp",EDGE,"E13.14.2"),sQuery(id+"F0.wireOp",EDGE,"E13.14.3"),sQuery(id+"F0.wireOp",EDGE,"E13.14.4"),sQuery(id+"F0.wireOp",EDGE,"E13.15.0"),sQuery(id+"F0.wireOp",EDGE,"E13.15.1"),sQuery(id+"F0.wireOp",EDGE,"E13.15.2"),sQuery(id+"F0.wireOp",EDGE,"E13.15.3"),sQuery(id+"F0.wireOp",EDGE,"E13.15.4"),sQuery(id+"F0.wireOp",EDGE,"E13.16.0"),sQuery(id+"F0.wireOp",EDGE,"E13.16.1"),sQuery(id+"F0.wireOp",EDGE,"E13.16.2"),sQuery(id+"F0.wireOp",EDGE,"E13.16.3"),sQuery(id+"F0.wireOp",EDGE,"E13.16.4"),sQuery(id+"F0.wireOp",EDGE,"E13.17.0"),sQuery(id+"F0.wireOp",EDGE,"E13.17.1"),sQuery(id+"F0.wireOp",EDGE,"E13.17.2"),sQuery(id+"F0.wireOp",EDGE,"E13.17.3"),sQuery(id+"F0.wireOp",EDGE,"E13.17.4"),sQuery(id+"F0.wireOp",EDGE,"E13.18.0"),sQuery(id+"F0.wireOp",EDGE,"E13.18.1"),sQuery(id+"F0.wireOp",EDGE,"E13.18.2"),sQuery(id+"F0.wireOp",EDGE,"E13.18.3"),sQuery(id+"F0.wireOp",EDGE,"E13.18.4"),sQuery(id+"F0.wireOp",EDGE,"E13.19.0"),sQuery(id+"F0.wireOp",EDGE,"E13.19.1"),sQuery(id+"F0.wireOp",EDGE,"E13.19.2"),sQuery(id+"F0.wireOp",EDGE,"E13.19.3"),sQuery(id+"F0.wireOp",EDGE,"E13.19.4"),sQuery(id+"F0.wireOp",EDGE,"E13.20.0"),sQuery(id+"F0.wireOp",EDGE,"E13.20.1"),sQuery(id+"F0.wireOp",EDGE,"E13.20.2"),sQuery(id+"F0.wireOp",EDGE,"E13.20.3"),sQuery(id+"F0.wireOp",EDGE,"E13.20.4"),sQuery(id+"F0.wireOp",EDGE,"E13.21.0"),sQuery(id+"F0.wireOp",EDGE,"E13.21.1"),sQuery(id+"F0.wireOp",EDGE,"E13.21.2"),sQuery(id+"F0.wireOp",EDGE,"E13.21.3"),sQuery(id+"F0.wireOp",EDGE,"E13.21.4"),sQuery(id+"F0.wireOp",EDGE,"E13.22.0"),sQuery(id+"F0.wireOp",EDGE,"E13.22.1"),sQuery(id+"F0.wireOp",EDGE,"E13.22.2"),sQuery(id+"F0.wireOp",EDGE,"E13.22.3"),sQuery(id+"F0.wireOp",EDGE,"E13.22.4"),sQuery(id+"F0.wireOp",EDGE,"E13.23.0"),sQuery(id+"F0.wireOp",EDGE,"E13.23.1"),sQuery(id+"F0.wireOp",EDGE,"E13.23.2"),sQuery(id+"F0.wireOp",EDGE,"E13.23.3"),sQuery(id+"F0.wireOp",EDGE,"E13.23.4")])]});
            hole(context, id + "F3", {"style" : HoleStyle.SIMPLE, "endStyle" : HoleEndStyle.THROUGH, "holeDiameter" : 3.8 * mm, "locations" : qUnion([Q0, Q1, Q2, Q3]), "scope" : qUnion([Q4]), "isTappedThrough" : true});
        }
        {
            var Q0;
            Q0=makeQuery(id+"F1.opExtrude","CAP_FACE",FACE,{"disambiguationData":[OSD([sQuery(id+"F0.wireOp",EDGE,"E0"),sQuery(id+"F0.wireOp",EDGE,"E8"),sQuery(id+"F0.wireOp",EDGE,"E9.MirrorCS"),sQuery(id+"F0.wireOp",EDGE,"E10"),sQuery(id+"F0.wireOp",EDGE,"E11"),sQuery(id+"F0.wireOp",EDGE,"E12"),sQuery(id+"F0.wireOp",EDGE,"E13.1.0"),sQuery(id+"F0.wireOp",EDGE,"E13.1.1"),sQuery(id+"F0.wireOp",EDGE,"E13.1.2"),sQuery(id+"F0.wireOp",EDGE,"E13.1.3"),sQuery(id+"F0.wireOp",EDGE,"E13.1.4"),sQuery(id+"F0.wireOp",EDGE,"E13.2.0"),sQuery(id+"F0.wireOp",EDGE,"E13.2.1"),sQuery(id+"F0.wireOp",EDGE,"E13.2.2"),sQuery(id+"F0.wireOp",EDGE,"E13.2.3"),sQuery(id+"F0.wireOp",EDGE,"E13.2.4"),sQuery(id+"F0.wireOp",EDGE,"E13.3.0"),sQuery(id+"F0.wireOp",EDGE,"E13.3.1"),sQuery(id+"F0.wireOp",EDGE,"E13.3.2"),sQuery(id+"F0.wireOp",EDGE,"E13.3.3"),sQuery(id+"F0.wireOp",EDGE,"E13.3.4"),sQuery(id+"F0.wireOp",EDGE,"E13.4.0"),sQuery(id+"F0.wireOp",EDGE,"E13.4.1"),sQuery(id+"F0.wireOp",EDGE,"E13.4.2"),sQuery(id+"F0.wireOp",EDGE,"E13.4.3"),sQuery(id+"F0.wireOp",EDGE,"E13.4.4"),sQuery(id+"F0.wireOp",EDGE,"E13.5.0"),sQuery(id+"F0.wireOp",EDGE,"E13.5.1"),sQuery(id+"F0.wireOp",EDGE,"E13.5.2"),sQuery(id+"F0.wireOp",EDGE,"E13.5.3"),sQuery(id+"F0.wireOp",EDGE,"E13.5.4"),sQuery(id+"F0.wireOp",EDGE,"E13.6.0"),sQuery(id+"F0.wireOp",EDGE,"E13.6.1"),sQuery(id+"F0.wireOp",EDGE,"E13.6.2"),sQuery(id+"F0.wireOp",EDGE,"E13.6.3"),sQuery(id+"F0.wireOp",EDGE,"E13.6.4"),sQuery(id+"F0.wireOp",EDGE,"E13.7.0"),sQuery(id+"F0.wireOp",EDGE,"E13.7.1"),sQuery(id+"F0.wireOp",EDGE,"E13.7.2"),sQuery(id+"F0.wireOp",EDGE,"E13.7.3"),sQuery(id+"F0.wireOp",EDGE,"E13.7.4"),sQuery(id+"F0.wireOp",EDGE,"E13.8.0"),sQuery(id+"F0.wireOp",EDGE,"E13.8.1"),sQuery(id+"F0.wireOp",EDGE,"E13.8.2"),sQuery(id+"F0.wireOp",EDGE,"E13.8.3"),sQuery(id+"F0.wireOp",EDGE,"E13.8.4"),sQuery(id+"F0.wireOp",EDGE,"E13.9.0"),sQuery(id+"F0.wireOp",EDGE,"E13.9.1"),sQuery(id+"F0.wireOp",EDGE,"E13.9.2"),sQuery(id+"F0.wireOp",EDGE,"E13.9.3"),sQuery(id+"F0.wireOp",EDGE,"E13.9.4"),sQuery(id+"F0.wireOp",EDGE,"E13.10.0"),sQuery(id+"F0.wireOp",EDGE,"E13.10.1"),sQuery(id+"F0.wireOp",EDGE,"E13.10.2"),sQuery(id+"F0.wireOp",EDGE,"E13.10.3"),sQuery(id+"F0.wireOp",EDGE,"E13.10.4"),sQuery(id+"F0.wireOp",EDGE,"E13.11.0"),sQuery(id+"F0.wireOp",EDGE,"E13.11.1"),sQuery(id+"F0.wireOp",EDGE,"E13.11.2"),sQuery(id+"F0.wireOp",EDGE,"E13.11.3"),sQuery(id+"F0.wireOp",EDGE,"E13.11.4"),sQuery(id+"F0.wireOp",EDGE,"E13.12.0"),sQuery(id+"F0.wireOp",EDGE,"E13.12.1"),sQuery(id+"F0.wireOp",EDGE,"E13.12.2"),sQuery(id+"F0.wireOp",EDGE,"E13.12.3"),sQuery(id+"F0.wireOp",EDGE,"E13.12.4"),sQuery(id+"F0.wireOp",EDGE,"E13.13.0"),sQuery(id+"F0.wireOp",EDGE,"E13.13.1"),sQuery(id+"F0.wireOp",EDGE,"E13.13.2"),sQuery(id+"F0.wireOp",EDGE,"E13.13.3"),sQuery(id+"F0.wireOp",EDGE,"E13.13.4"),sQuery(id+"F0.wireOp",EDGE,"E13.14.0"),sQuery(id+"F0.wireOp",EDGE,"E13.14.1"),sQuery(id+"F0.wireOp",EDGE,"E13.14.2"),sQuery(id+"F0.wireOp",EDGE,"E13.14.3"),sQuery(id+"F0.wireOp",EDGE,"E13.14.4"),sQuery(id+"F0.wireOp",EDGE,"E13.15.0"),sQuery(id+"F0.wireOp",EDGE,"E13.15.1"),sQuery(id+"F0.wireOp",EDGE,"E13.15.2"),sQuery(id+"F0.wireOp",EDGE,"E13.15.3"),sQuery(id+"F0.wireOp",EDGE,"E13.15.4"),sQuery(id+"F0.wireOp",EDGE,"E13.16.0"),sQuery(id+"F0.wireOp",EDGE,"E13.16.1"),sQuery(id+"F0.wireOp",EDGE,"E13.16.2"),sQuery(id+"F0.wireOp",EDGE,"E13.16.3"),sQuery(id+"F0.wireOp",EDGE,"E13.16.4"),sQuery(id+"F0.wireOp",EDGE,"E13.17.0"),sQuery(id+"F0.wireOp",EDGE,"E13.17.1"),sQuery(id+"F0.wireOp",EDGE,"E13.17.2"),sQuery(id+"F0.wireOp",EDGE,"E13.17.3"),sQuery(id+"F0.wireOp",EDGE,"E13.17.4"),sQuery(id+"F0.wireOp",EDGE,"E13.18.0"),sQuery(id+"F0.wireOp",EDGE,"E13.18.1"),sQuery(id+"F0.wireOp",EDGE,"E13.18.2"),sQuery(id+"F0.wireOp",EDGE,"E13.18.3"),sQuery(id+"F0.wireOp",EDGE,"E13.18.4"),sQuery(id+"F0.wireOp",EDGE,"E13.19.0"),sQuery(id+"F0.wireOp",EDGE,"E13.19.1"),sQuery(id+"F0.wireOp",EDGE,"E13.19.2"),sQuery(id+"F0.wireOp",EDGE,"E13.19.3"),sQuery(id+"F0.wireOp",EDGE,"E13.19.4"),sQuery(id+"F0.wireOp",EDGE,"E13.20.0"),sQuery(id+"F0.wireOp",EDGE,"E13.20.1"),sQuery(id+"F0.wireOp",EDGE,"E13.20.2"),sQuery(id+"F0.wireOp",EDGE,"E13.20.3"),sQuery(id+"F0.wireOp",EDGE,"E13.20.4"),sQuery(id+"F0.wireOp",EDGE,"E13.21.0"),sQuery(id+"F0.wireOp",EDGE,"E13.21.1"),sQuery(id+"F0.wireOp",EDGE,"E13.21.2"),sQuery(id+"F0.wireOp",EDGE,"E13.21.3"),sQuery(id+"F0.wireOp",EDGE,"E13.21.4"),sQuery(id+"F0.wireOp",EDGE,"E13.22.0"),sQuery(id+"F0.wireOp",EDGE,"E13.22.1"),sQuery(id+"F0.wireOp",EDGE,"E13.22.2"),sQuery(id+"F0.wireOp",EDGE,"E13.22.3"),sQuery(id+"F0.wireOp",EDGE,"E13.22.4"),sQuery(id+"F0.wireOp",EDGE,"E13.23.0"),sQuery(id+"F0.wireOp",EDGE,"E13.23.1"),sQuery(id+"F0.wireOp",EDGE,"E13.23.2"),sQuery(id+"F0.wireOp",EDGE,"E13.23.3"),sQuery(id+"F0.wireOp",EDGE,"E13.23.4")])],"isStart":false});
            var sketch = newSketch(context, id + "F4", { "sketchPlane" : qUnion([Q0])});
            skPoint(sketch, "E19", {"position": v(0, 0) * mm});
            skSolve(sketch);
        }
        {
            var Q0;
            Q0=sQuery(id+"F4.wireOp",VERTEX,"E19");
            var Q1;
            Q1=makeQuery(id+"F1.opExtrude","SWEPT_BODY",BODY,{"disambiguationData":[OSD([sQuery(id+"F0.wireOp",EDGE,"E0"),sQuery(id+"F0.wireOp",EDGE,"E8"),sQuery(id+"F0.wireOp",EDGE,"E9.MirrorCS"),sQuery(id+"F0.wireOp",EDGE,"E10"),sQuery(id+"F0.wireOp",EDGE,"E11"),sQuery(id+"F0.wireOp",EDGE,"E12"),sQuery(id+"F0.wireOp",EDGE,"E13.1.0"),sQuery(id+"F0.wireOp",EDGE,"E13.1.1"),sQuery(id+"F0.wireOp",EDGE,"E13.1.2"),sQuery(id+"F0.wireOp",EDGE,"E13.1.3"),sQuery(id+"F0.wireOp",EDGE,"E13.1.4"),sQuery(id+"F0.wireOp",EDGE,"E13.2.0"),sQuery(id+"F0.wireOp",EDGE,"E13.2.1"),sQuery(id+"F0.wireOp",EDGE,"E13.2.2"),sQuery(id+"F0.wireOp",EDGE,"E13.2.3"),sQuery(id+"F0.wireOp",EDGE,"E13.2.4"),sQuery(id+"F0.wireOp",EDGE,"E13.3.0"),sQuery(id+"F0.wireOp",EDGE,"E13.3.1"),sQuery(id+"F0.wireOp",EDGE,"E13.3.2"),sQuery(id+"F0.wireOp",EDGE,"E13.3.3"),sQuery(id+"F0.wireOp",EDGE,"E13.3.4"),sQuery(id+"F0.wireOp",EDGE,"E13.4.0"),sQuery(id+"F0.wireOp",EDGE,"E13.4.1"),sQuery(id+"F0.wireOp",EDGE,"E13.4.2"),sQuery(id+"F0.wireOp",EDGE,"E13.4.3"),sQuery(id+"F0.wireOp",EDGE,"E13.4.4"),sQuery(id+"F0.wireOp",EDGE,"E13.5.0"),sQuery(id+"F0.wireOp",EDGE,"E13.5.1"),sQuery(id+"F0.wireOp",EDGE,"E13.5.2"),sQuery(id+"F0.wireOp",EDGE,"E13.5.3"),sQuery(id+"F0.wireOp",EDGE,"E13.5.4"),sQuery(id+"F0.wireOp",EDGE,"E13.6.0"),sQuery(id+"F0.wireOp",EDGE,"E13.6.1"),sQuery(id+"F0.wireOp",EDGE,"E13.6.2"),sQuery(id+"F0.wireOp",EDGE,"E13.6.3"),sQuery(id+"F0.wireOp",EDGE,"E13.6.4"),sQuery(id+"F0.wireOp",EDGE,"E13.7.0"),sQuery(id+"F0.wireOp",EDGE,"E13.7.1"),sQuery(id+"F0.wireOp",EDGE,"E13.7.2"),sQuery(id+"F0.wireOp",EDGE,"E13.7.3"),sQuery(id+"F0.wireOp",EDGE,"E13.7.4"),sQuery(id+"F0.wireOp",EDGE,"E13.8.0"),sQuery(id+"F0.wireOp",EDGE,"E13.8.1"),sQuery(id+"F0.wireOp",EDGE,"E13.8.2"),sQuery(id+"F0.wireOp",EDGE,"E13.8.3"),sQuery(id+"F0.wireOp",EDGE,"E13.8.4"),sQuery(id+"F0.wireOp",EDGE,"E13.9.0"),sQuery(id+"F0.wireOp",EDGE,"E13.9.1"),sQuery(id+"F0.wireOp",EDGE,"E13.9.2"),sQuery(id+"F0.wireOp",EDGE,"E13.9.3"),sQuery(id+"F0.wireOp",EDGE,"E13.9.4"),sQuery(id+"F0.wireOp",EDGE,"E13.10.0"),sQuery(id+"F0.wireOp",EDGE,"E13.10.1"),sQuery(id+"F0.wireOp",EDGE,"E13.10.2"),sQuery(id+"F0.wireOp",EDGE,"E13.10.3"),sQuery(id+"F0.wireOp",EDGE,"E13.10.4"),sQuery(id+"F0.wireOp",EDGE,"E13.11.0"),sQuery(id+"F0.wireOp",EDGE,"E13.11.1"),sQuery(id+"F0.wireOp",EDGE,"E13.11.2"),sQuery(id+"F0.wireOp",EDGE,"E13.11.3"),sQuery(id+"F0.wireOp",EDGE,"E13.11.4"),sQuery(id+"F0.wireOp",EDGE,"E13.12.0"),sQuery(id+"F0.wireOp",EDGE,"E13.12.1"),sQuery(id+"F0.wireOp",EDGE,"E13.12.2"),sQuery(id+"F0.wireOp",EDGE,"E13.12.3"),sQuery(id+"F0.wireOp",EDGE,"E13.12.4"),sQuery(id+"F0.wireOp",EDGE,"E13.13.0"),sQuery(id+"F0.wireOp",EDGE,"E13.13.1"),sQuery(id+"F0.wireOp",EDGE,"E13.13.2"),sQuery(id+"F0.wireOp",EDGE,"E13.13.3"),sQuery(id+"F0.wireOp",EDGE,"E13.13.4"),sQuery(id+"F0.wireOp",EDGE,"E13.14.0"),sQuery(id+"F0.wireOp",EDGE,"E13.14.1"),sQuery(id+"F0.wireOp",EDGE,"E13.14.2"),sQuery(id+"F0.wireOp",EDGE,"E13.14.3"),sQuery(id+"F0.wireOp",EDGE,"E13.14.4"),sQuery(id+"F0.wireOp",EDGE,"E13.15.0"),sQuery(id+"F0.wireOp",EDGE,"E13.15.1"),sQuery(id+"F0.wireOp",EDGE,"E13.15.2"),sQuery(id+"F0.wireOp",EDGE,"E13.15.3"),sQuery(id+"F0.wireOp",EDGE,"E13.15.4"),sQuery(id+"F0.wireOp",EDGE,"E13.16.0"),sQuery(id+"F0.wireOp",EDGE,"E13.16.1"),sQuery(id+"F0.wireOp",EDGE,"E13.16.2"),sQuery(id+"F0.wireOp",EDGE,"E13.16.3"),sQuery(id+"F0.wireOp",EDGE,"E13.16.4"),sQuery(id+"F0.wireOp",EDGE,"E13.17.0"),sQuery(id+"F0.wireOp",EDGE,"E13.17.1"),sQuery(id+"F0.wireOp",EDGE,"E13.17.2"),sQuery(id+"F0.wireOp",EDGE,"E13.17.3"),sQuery(id+"F0.wireOp",EDGE,"E13.17.4"),sQuery(id+"F0.wireOp",EDGE,"E13.18.0"),sQuery(id+"F0.wireOp",EDGE,"E13.18.1"),sQuery(id+"F0.wireOp",EDGE,"E13.18.2"),sQuery(id+"F0.wireOp",EDGE,"E13.18.3"),sQuery(id+"F0.wireOp",EDGE,"E13.18.4"),sQuery(id+"F0.wireOp",EDGE,"E13.19.0"),sQuery(id+"F0.wireOp",EDGE,"E13.19.1"),sQuery(id+"F0.wireOp",EDGE,"E13.19.2"),sQuery(id+"F0.wireOp",EDGE,"E13.19.3"),sQuery(id+"F0.wireOp",EDGE,"E13.19.4"),sQuery(id+"F0.wireOp",EDGE,"E13.20.0"),sQuery(id+"F0.wireOp",EDGE,"E13.20.1"),sQuery(id+"F0.wireOp",EDGE,"E13.20.2"),sQuery(id+"F0.wireOp",EDGE,"E13.20.3"),sQuery(id+"F0.wireOp",EDGE,"E13.20.4"),sQuery(id+"F0.wireOp",EDGE,"E13.21.0"),sQuery(id+"F0.wireOp",EDGE,"E13.21.1"),sQuery(id+"F0.wireOp",EDGE,"E13.21.2"),sQuery(id+"F0.wireOp",EDGE,"E13.21.3"),sQuery(id+"F0.wireOp",EDGE,"E13.21.4"),sQuery(id+"F0.wireOp",EDGE,"E13.22.0"),sQuery(id+"F0.wireOp",EDGE,"E13.22.1"),sQuery(id+"F0.wireOp",EDGE,"E13.22.2"),sQuery(id+"F0.wireOp",EDGE,"E13.22.3"),sQuery(id+"F0.wireOp",EDGE,"E13.22.4"),sQuery(id+"F0.wireOp",EDGE,"E13.23.0"),sQuery(id+"F0.wireOp",EDGE,"E13.23.1"),sQuery(id+"F0.wireOp",EDGE,"E13.23.2"),sQuery(id+"F0.wireOp",EDGE,"E13.23.3"),sQuery(id+"F0.wireOp",EDGE,"E13.23.4")])]});
            hole(context, id + "F5", {"style" : HoleStyle.SIMPLE, "endStyle" : HoleEndStyle.THROUGH, "holeDiameter" : 7.62 * mm, "locations" : qUnion([Q0]), "scope" : qUnion([Q1]), "isTappedThrough" : true});
        }
    });
